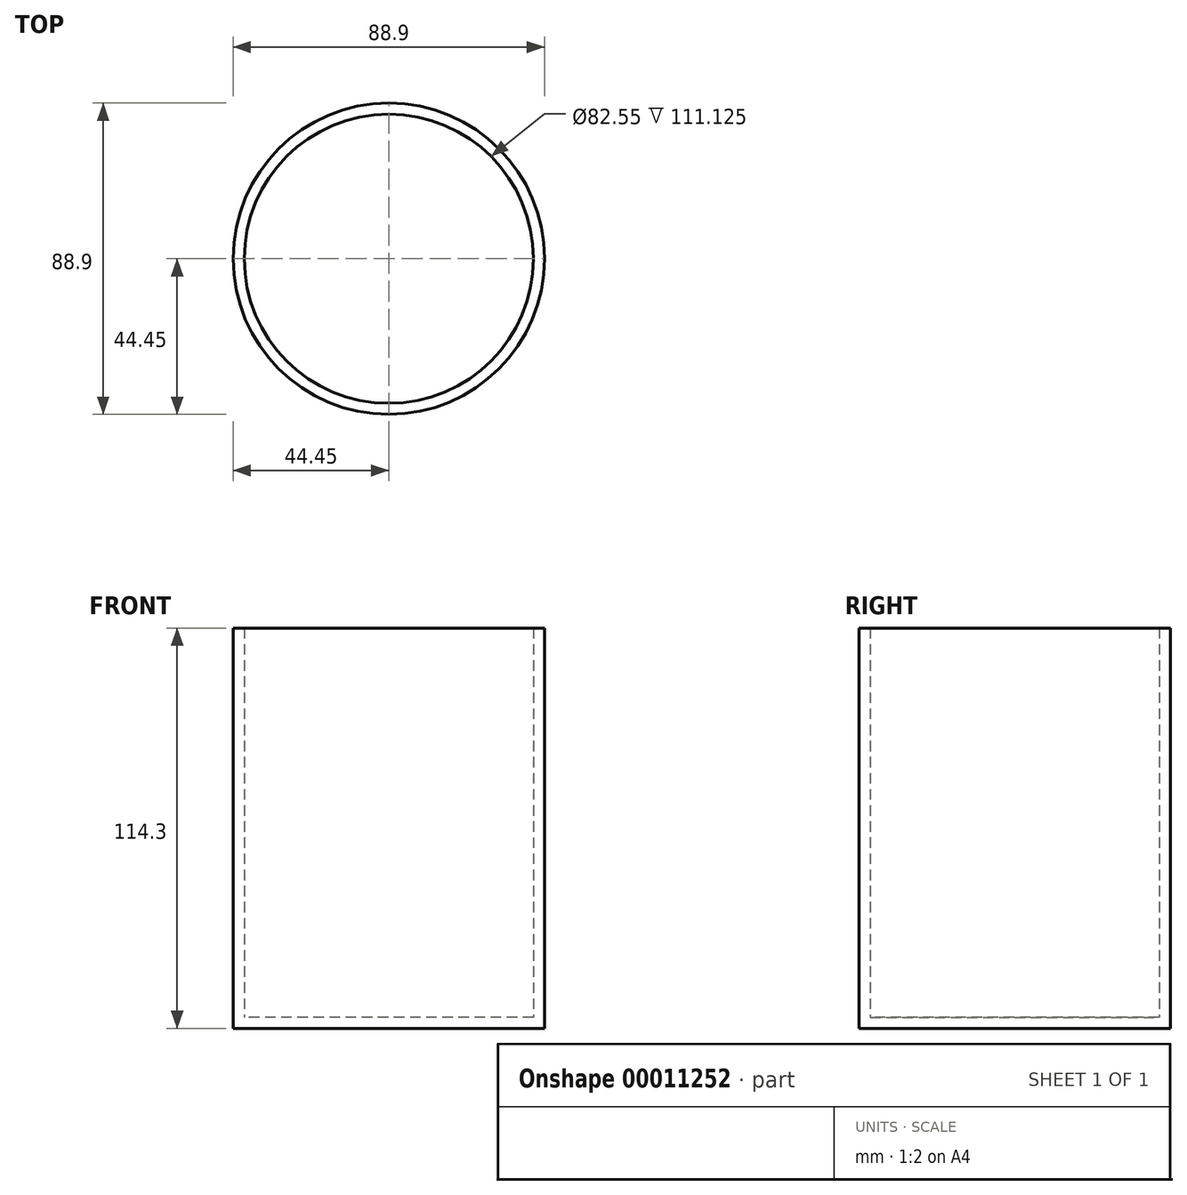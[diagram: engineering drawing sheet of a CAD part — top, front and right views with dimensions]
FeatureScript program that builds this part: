
annotation { "Feature Type Name" : "Feature", "Feature Type Description" : "" }
export const myFeature = defineFeature(function(context is Context, id is Id, definition is map)
    precondition{}
    {
        {
            var Q0;
            Q0=qCreatedBy(makeId("Top.planeOp"),FACE);
            var sketch = newSketch(context, id + "F0", { "sketchPlane" : qUnion([Q0])});
            skCircle(sketch, "E0", {"center": v(0, 0) * mm, "radius": 44.45 * mm});
            skSolve(sketch);
        }
        {
            var Q0;
            Q0=makeQuery(id+"F0.imprint","IMPRINT",FACE,{"disambiguationData":[TD([[makeQuery(id+"F0.imprint","IMPRINT",EDGE,{"derivedFrom":sQuery(id+"F0.wireOp",EDGE,"E0")}),1.0]])]});
            extrude(context, id + "F1", {"entities" : qUnion([Q0]), "depth" : 114.3 * mm});
        }
        {
            var Q0;
            Q0=makeQuery(id+"F1.opExtrude","CAP_FACE",FACE,{"disambiguationData":[OSD([sQuery(id+"F0.wireOp",EDGE,"E0")])],"isStart":false});
            shell(context, id + "F2", {"entities" : qUnion([Q0]), "thickness" : 3.17 * mm});
        }
    });
